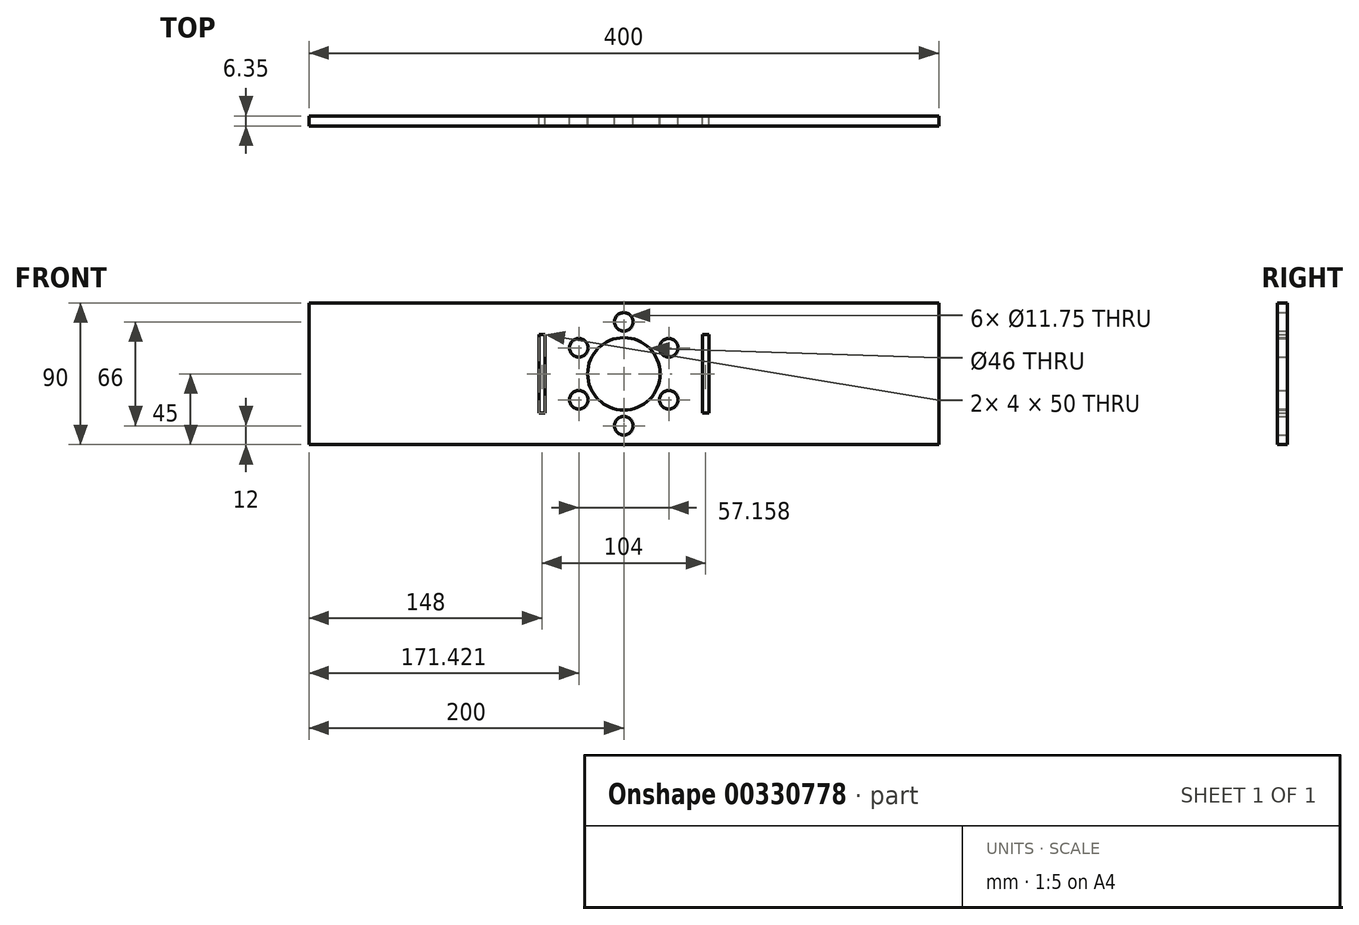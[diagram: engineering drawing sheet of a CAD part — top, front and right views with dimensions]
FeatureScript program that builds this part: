
annotation { "Feature Type Name" : "Feature", "Feature Type Description" : "" }
export const myFeature = defineFeature(function(context is Context, id is Id, definition is map)
    precondition{}
    {
        {
            var Q0;
            Q0=qCreatedBy(makeId("Front.planeOp"),FACE);
            var sketch = newSketch(context, id + "F0", { "sketchPlane" : qUnion([Q0])});
            skLineSegment(sketch, "E0.bottom", {"start": v(200, -45) * mm, "end": v(-200, -45) * mm});
            skLineSegment(sketch, "E0.top", {"start": v(200, 45) * mm, "end": v(-200, 45) * mm});
            skLineSegment(sketch, "E0.left", {"start": v(200, -45) * mm, "end": v(200, 45) * mm});
            skLineSegment(sketch, "E0.right", {"start": v(-200, -45) * mm, "end": v(-200, 45) * mm});
            skPoint(sketch, "E0.middle", {"position": v(0, 0) * mm});
            skCircle(sketch, "E1", {"center": v(0, 0) * mm, "radius": 23 * mm});
            skCircle(sketch, "E2", {"center": v(0, 0) * mm, "radius": 33 * mm});
            skCircle(sketch, "E3", {"center": v(0, 33) * mm, "radius": 5.87 * mm});
            skCircle(sketch, "E4.1.0", {"center": v(-28.58, 16.5) * mm, "radius": 5.87 * mm});
            skCircle(sketch, "E4.2.0", {"center": v(-28.58, -16.5) * mm, "radius": 5.87 * mm});
            skCircle(sketch, "E4.3.0", {"center": v(0, -33) * mm, "radius": 5.87 * mm});
            skCircle(sketch, "E4.4.0", {"center": v(28.58, -16.5) * mm, "radius": 5.87 * mm});
            skCircle(sketch, "E4.5.0", {"center": v(28.58, 16.5) * mm, "radius": 5.87 * mm});
            skLineSegment(sketch, "E5.right", {"start": v(-50, -25) * mm, "end": v(-50, 25) * mm});
            skLineSegment(sketch, "E6", {"start": v(50, 25) * mm, "end": v(50, -25) * mm});
            skLineSegment(sketch, "E7.bottom", {"start": v(-50, 25) * mm, "end": v(-54, 25) * mm});
            skLineSegment(sketch, "E7.top", {"start": v(-50, -25) * mm, "end": v(-54, -25) * mm});
            skLineSegment(sketch, "E7.left", {"start": v(-50, 25) * mm, "end": v(-50, -25) * mm});
            skLineSegment(sketch, "E7.right", {"start": v(-54, 25) * mm, "end": v(-54, -25) * mm});
            skLineSegment(sketch, "E8.bottom", {"start": v(50, 25) * mm, "end": v(54, 25) * mm});
            skLineSegment(sketch, "E8.top", {"start": v(50, -25) * mm, "end": v(54, -25) * mm});
            skLineSegment(sketch, "E8.right", {"start": v(54, 25) * mm, "end": v(54, -25) * mm});
            skSolve(sketch);
        }
        {
            var Q0;
            Q0=makeQuery(id+"F0.imprint","IMPRINT",FACE,{"disambiguationData":[TD([[makeQuery(id+"F0.imprint","IMPRINT",EDGE,{"derivedFrom":sQuery(id+"F0.wireOp",EDGE,"E0.bottom")}),-1.0]])]});
            var Q1;
            Q1=makeQuery(id+"F0.imprint","IMPRINT",FACE,{"disambiguationData":[TD([[makeQuery(id+"F0.imprint","IMPRINT",EDGE,{"derivedFrom":sQuery(id+"F0.wireOp",EDGE,"E1")}),-1.0]])]});
            extrude(context, id + "F1", {"entities" : qUnion([Q0, Q1]), "depth" : 6.35 * mm});
        }
    });
